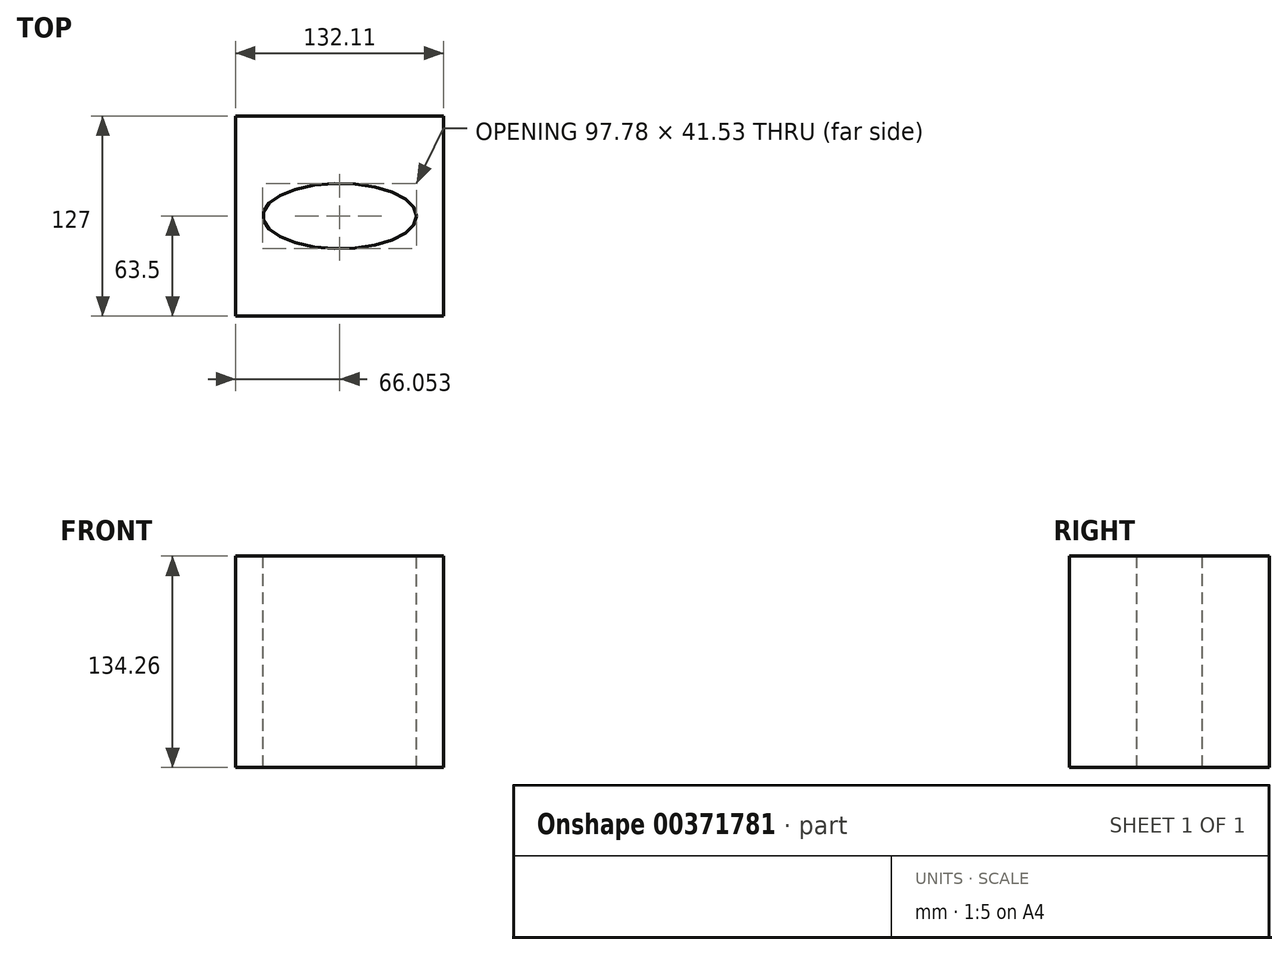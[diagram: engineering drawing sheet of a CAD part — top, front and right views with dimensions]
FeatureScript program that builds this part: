
annotation { "Feature Type Name" : "Feature", "Feature Type Description" : "" }
export const myFeature = defineFeature(function(context is Context, id is Id, definition is map)
    precondition{}
    {
        {
            var Q0;
            Q0=qCreatedBy(makeId("Top.planeOp"),FACE);
            var sketch = newSketch(context, id + "F0", { "sketchPlane" : qUnion([Q0])});
            skLineSegment(sketch, "E0.bottom", {"start": v(-96.53, -127) * mm, "end": v(35.58, -127) * mm});
            skLineSegment(sketch, "E0.top", {"start": v(-96.53, 0) * mm, "end": v(35.58, 0) * mm});
            skLineSegment(sketch, "E0.left", {"start": v(-96.53, -127) * mm, "end": v(-96.53, 0) * mm});
            skLineSegment(sketch, "E0.right", {"start": v(35.58, -127) * mm, "end": v(35.58, 0) * mm});
            skSolve(sketch);
        }
        {
            var Q0;
            Q0=makeQuery(id+"F0.imprint","IMPRINT",FACE,{"disambiguationData":[TD([[makeQuery(id+"F0.imprint","IMPRINT",EDGE,{"derivedFrom":sQuery(id+"F0.wireOp",EDGE,"E0.bottom")}),1.0]])]});
            extrude(context, id + "F1", {"entities" : qUnion([Q0]), "depth" : 134.26 * mm});
        }
        {
            var Q0;
            Q0=makeQuery(id+"F1.opExtrude","CAP_FACE",FACE,{"disambiguationData":[OSD([sQuery(id+"F0.wireOp",EDGE,"E0.bottom"),sQuery(id+"F0.wireOp",EDGE,"E0.top"),sQuery(id+"F0.wireOp",EDGE,"E0.left"),sQuery(id+"F0.wireOp",EDGE,"E0.right")])],"isStart":false});
            var sketch = newSketch(context, id + "F2", { "sketchPlane" : qUnion([Q0])});
            skEllipse(sketch, "E1", {"center": v(-30.48, -63.5) * mm, "majorRadius": 48.89 * mm, "minorRadius": 20.77 * mm, "majorAxis": v(1, 0)});
            skPoint(sketch, "E1.centerSnap0", {"position": v(35.58, -63.5) * mm});
            skPoint(sketch, "E1.centerSnap1", {"position": v(-30.48, 0) * mm});
            skSolve(sketch);
        }
        {
            var Q0;
            Q0 = qSketchRegion(id + "F2", true);
            var Q1;
            Q1=makeQuery(id+"F2.imprint","IMPRINT",FACE,{"disambiguationData":[TD([[makeQuery(id+"F2.imprint","IMPRINT",EDGE,{"derivedFrom":sQuery(id+"F2.wireOp",EDGE,"E1")}),1.0]])]});
            extrude(context, id + "F3", {"entities" : qUnion([Q0, Q1]), "operationType" : NewBodyOperationType.REMOVE, "endBound" : BoundingType.THROUGH_ALL, "oppositeDirection" : true, "depth" : 25.4 * mm});
        }
    });
